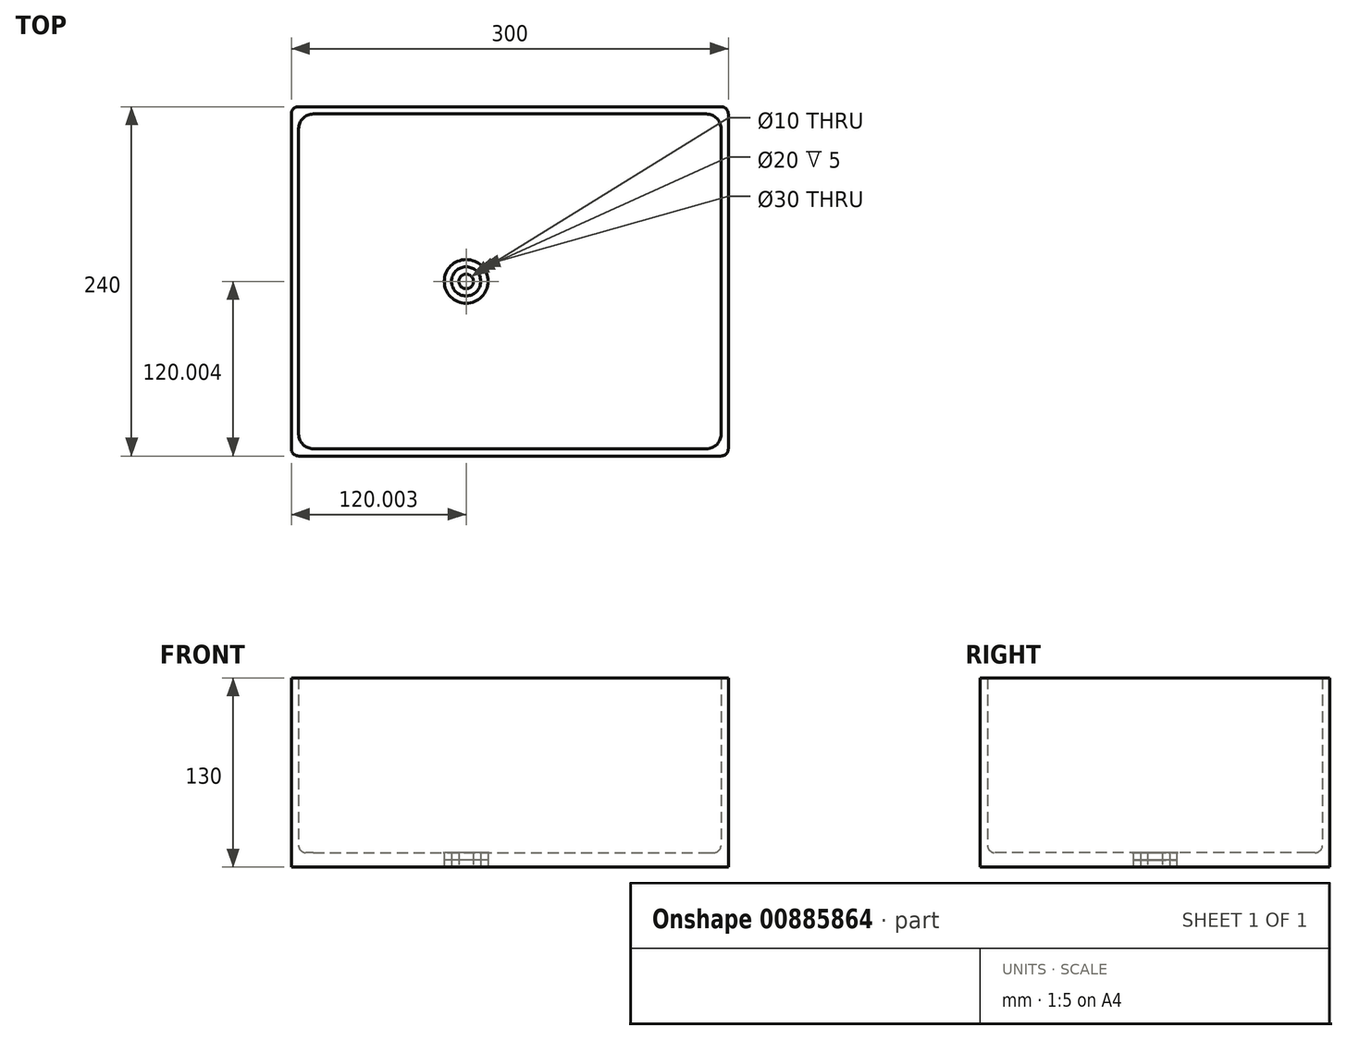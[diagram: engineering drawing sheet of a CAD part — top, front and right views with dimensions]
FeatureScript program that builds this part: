
annotation { "Feature Type Name" : "Feature", "Feature Type Description" : "" }
export const myFeature = defineFeature(function(context is Context, id is Id, definition is map)
    precondition{}
    {
        {
            var Q0;
            Q0=qCreatedBy(makeId("Top.planeOp"),FACE);
            var sketch = newSketch(context, id + "F0", { "sketchPlane" : qUnion([Q0])});
            skLineSegment(sketch, "E0.bottom", {"start": v(-127.94, 163.12) * mm, "end": v(92.06, 163.12) * mm});
            skLineSegment(sketch, "E0.top", {"start": v(-127.94, -66.88) * mm, "end": v(92.06, -66.88) * mm});
            skLineSegment(sketch, "E0.left", {"start": v(-137.94, 153.12) * mm, "end": v(-137.94, -56.88) * mm});
            skLineSegment(sketch, "E1.1", {"start": v(-142.94, 163.12) * mm, "end": v(-142.94, -66.88) * mm});
            skLineSegment(sketch, "E2", {"start": v(-137.94, 168.12) * mm, "end": v(152.06, 168.12) * mm});
            skLineSegment(sketch, "E3", {"start": v(-137.94, -71.88) * mm, "end": v(152.06, -71.88) * mm});
            skLineSegment(sketch, "E4", {"start": v(157.06, 163.12) * mm, "end": v(157.06, -66.88) * mm});
            skLineSegment(sketch, "E5", {"start": v(92.06, 163.12) * mm, "end": v(142.06, 163.12) * mm});
            skLineSegment(sketch, "E6", {"start": v(92.06, -66.88) * mm, "end": v(142.06, -66.88) * mm});
            skLineSegment(sketch, "E7", {"start": v(152.06, 153.12) * mm, "end": v(152.06, -56.88) * mm});
            skPoint(sketch, "E8.visualSharp", {"position": v(-137.94, 163.12) * mm});
            skArc(sketch, "E8.filletArc", {"start": v(-127.94, 163.12) * mm, "mid": v(-135, 160.2) * mm, "end": v(-137.94, 153.12) * mm});
            skPoint(sketch, "E9.visualSharp", {"position": v(-137.94, -66.88) * mm});
            skArc(sketch, "E9.filletArc", {"start": v(-137.94, -56.88) * mm, "mid": v(-135, -63.95) * mm, "end": v(-127.94, -66.88) * mm});
            skPoint(sketch, "E10.visualSharp", {"position": v(152.06, -66.88) * mm});
            skArc(sketch, "E10.filletArc", {"start": v(142.06, -66.88) * mm, "mid": v(149.13, -63.95) * mm, "end": v(152.06, -56.88) * mm});
            skPoint(sketch, "E11.visualSharp", {"position": v(152.06, 163.12) * mm});
            skArc(sketch, "E11.filletArc", {"start": v(152.06, 153.12) * mm, "mid": v(149.13, 160.2) * mm, "end": v(142.06, 163.12) * mm});
            skPoint(sketch, "E12.visualSharp", {"position": v(-142.94, 168.12) * mm});
            skArc(sketch, "E12.filletArc", {"start": v(-137.94, 168.12) * mm, "mid": v(-141.47, 166.66) * mm, "end": v(-142.94, 163.12) * mm});
            skPoint(sketch, "E13.visualSharp", {"position": v(157.06, 168.12) * mm});
            skArc(sketch, "E13.filletArc", {"start": v(157.06, 163.12) * mm, "mid": v(155.6, 166.66) * mm, "end": v(152.06, 168.12) * mm});
            skPoint(sketch, "E14.visualSharp", {"position": v(157.06, -71.88) * mm});
            skArc(sketch, "E14.filletArc", {"start": v(152.06, -71.88) * mm, "mid": v(155.6, -70.41) * mm, "end": v(157.06, -66.88) * mm});
            skPoint(sketch, "E15.visualSharp", {"position": v(-142.94, -71.88) * mm});
            skArc(sketch, "E15.filletArc", {"start": v(-142.94, -66.88) * mm, "mid": v(-141.47, -70.41) * mm, "end": v(-137.94, -71.88) * mm});
            skLineSegment(sketch, "E16", {"start": v(92.06, 163.12) * mm, "end": v(92.06, -66.88) * mm});
            skLineSegment(sketch, "E17", {"start": v(-137.94, 163.12) * mm, "end": v(92.06, 163.12) * mm});
            skLineSegment(sketch, "E18", {"start": v(-22.94, 163.12) * mm, "end": v(-22.94, 48.12) * mm, "construction": true});
            skPoint(sketch, "E18.endSnap0", {"position": v(-137.94, 48.12) * mm});
            skCircle(sketch, "E19", {"center": v(-22.94, 48.12) * mm, "radius": 15 * mm});
            skCircle(sketch, "E20", {"center": v(-22.94, 48.12) * mm, "radius": 5 * mm});
            skCircle(sketch, "E21.0", {"center": v(-22.94, 48.12) * mm, "radius": 10 * mm});
            skSolve(sketch);
        }
        {
            var Q0;
            Q0=makeQuery(id+"F0.imprint","IMPRINT",FACE,{"disambiguationData":[TD([[makeQuery(id+"F0.imprint","IMPRINT",EDGE,{"derivedFrom":sQuery(id+"F0.wireOp",EDGE,"E0.bottom")}),1.0]])]});
            var Q1;
            Q1=makeQuery(id+"F0.imprint","IMPRINT",FACE,{"disambiguationData":[TD([[makeQuery(id+"F0.imprint","IMPRINT",EDGE,{"derivedFrom":sQuery(id+"F0.wireOp",EDGE,"E0.bottom")}),1.0]])]});
            extrude(context, id + "F1", {"entities" : qUnion([Q0, Q1]), "depth" : 130 * mm, "offsetDistance" : 25 * mm});
        }
        {
            var Q0;
            Q0=makeQuery(id+"F0.imprint","IMPRINT",FACE,{"disambiguationData":[TD([[makeQuery(id+"F0.imprint","IMPRINT",EDGE,{"derivedFrom":sQuery(id+"F0.wireOp",EDGE,"E0.bottom")}),-1.0]])]});
            var Q1;
            Q1=makeQuery(id+"F0.imprint","IMPRINT",FACE,{"disambiguationData":[TD([[makeQuery(id+"F0.imprint","IMPRINT",EDGE,{"derivedFrom":sQuery(id+"F0.wireOp",EDGE,"E0.bottom")}),-1.0]])]});
            var Q2;
            Q2=makeQuery(id+"F0.imprint","IMPRINT",FACE,{"disambiguationData":[TD([[makeQuery(id+"F0.imprint","IMPRINT",EDGE,{"derivedFrom":sQuery(id+"F0.wireOp",EDGE,"E5")}),-1.0]])]});
            var Q3;
            Q3=makeQuery(id+"F0.imprint","IMPRINT",FACE,{"disambiguationData":[TD([[makeQuery(id+"F0.imprint","IMPRINT",EDGE,{"derivedFrom":sQuery(id+"F0.wireOp",EDGE,"E20")}),-1.0]])]});
            extrude(context, id + "F2", {"entities" : qUnion([Q0, Q1, Q2, Q3]), "operationType" : NewBodyOperationType.ADD, "depth" : 10 * mm, "offsetDistance" : 25 * mm});
        }
        {
            var Q0;
            Q0=makeQuery(id+"F0.imprint","IMPRINT",FACE,{"disambiguationData":[TD([[makeQuery(id+"F0.imprint","IMPRINT",EDGE,{"derivedFrom":sQuery(id+"F0.wireOp",EDGE,"E19")}),1.0]])]});
            extrude(context, id + "F3", {"entities" : qUnion([Q0]), "depth" : 5 * mm, "offsetDistance" : 25 * mm});
        }
        {
            var Q0;
            Q0=makeQuery(id+"F2.opExtrude","CAP_EDGE",EDGE,{"disambiguationData":[OSD([sQuery(id+"F0.wireOp",EDGE,"E21.0")])],"isStart":false});
            var Q1;
            Q1=makeQuery(id+"F2.opExtrude","CAP_EDGE",EDGE,{"disambiguationData":[OSD([sQuery(id+"F0.wireOp",EDGE,"E20")])],"isStart":false});
            var Q2;
            Q2=makeQuery(id+"F2.opExtrude","CAP_EDGE",EDGE,{"disambiguationData":[OSD([sQuery(id+"F0.wireOp",EDGE,"E19")])],"isStart":false});
            fillet(context, id + "F4", {"entities" : qUnion([Q0, Q1, Q2]), "radius" : .8 * mm, "tangentPropagation" : true, "allowEdgeOverflow" : false});
        }
        {
            var Q0;
            Q0=makeQuery(id+"F2.opExtrude","CAP_FACE",FACE,{"disambiguationData":[OSD([sQuery(id+"F0.wireOp",EDGE,"E0.bottom"),sQuery(id+"F0.wireOp",EDGE,"E0.top"),sQuery(id+"F0.wireOp",EDGE,"E0.left"),sQuery(id+"F0.wireOp",EDGE,"E5"),sQuery(id+"F0.wireOp",EDGE,"E6"),sQuery(id+"F0.wireOp",EDGE,"E7"),sQuery(id+"F0.wireOp",EDGE,"E8.filletArc"),sQuery(id+"F0.wireOp",EDGE,"E9.filletArc"),sQuery(id+"F0.wireOp",EDGE,"E10.filletArc"),sQuery(id+"F0.wireOp",EDGE,"E11.filletArc"),sQuery(id+"F0.wireOp",EDGE,"E19")])],"isStart":false});
            fillet(context, id + "F5", {"entities" : qUnion([Q0]), "radius" : 5 * mm, "tangentPropagation" : true, "allowEdgeOverflow" : false});
        }
    });
